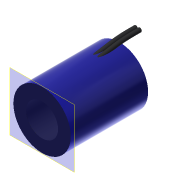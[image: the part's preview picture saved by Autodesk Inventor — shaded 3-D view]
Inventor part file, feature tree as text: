
AUTODESK INVENTOR PART (.ipt)
format: ipt  version: 2018.1 (Build 221171000, 171)  size: 157,184 bytes
history: native  units: mm
features: other x6, sketch x3, extrude x1, sweep x1
ambient origin geometry x8: Origin, YZ Plane, XZ Plane, XY Plane, X Axis, Y Axis, Z Axis, Center Point
bodies: Body1 (feature_tree)
feature tree (11):
  other  "Твердое тело1"
  other  "РабПлоскость1"
  sketch  "Эскиз1"
  other  "РабПлоскость2"
  extrude  "Выдавливание1"  Depth=21.5mm
  sweep  "Сдвиг1"
  sketch  "Эскиз2"
  sketch  "3D эскиз1"
  parser-record x1  (decoder bookkeeping rows leaked as tree rows — omitted from the tree; the rows remain in map.json)
  other  "0837 solenoid.iam"
  other  "frame:1"
note: 1 file-system path scrubbed to <path> (originals preserved in map.json)
